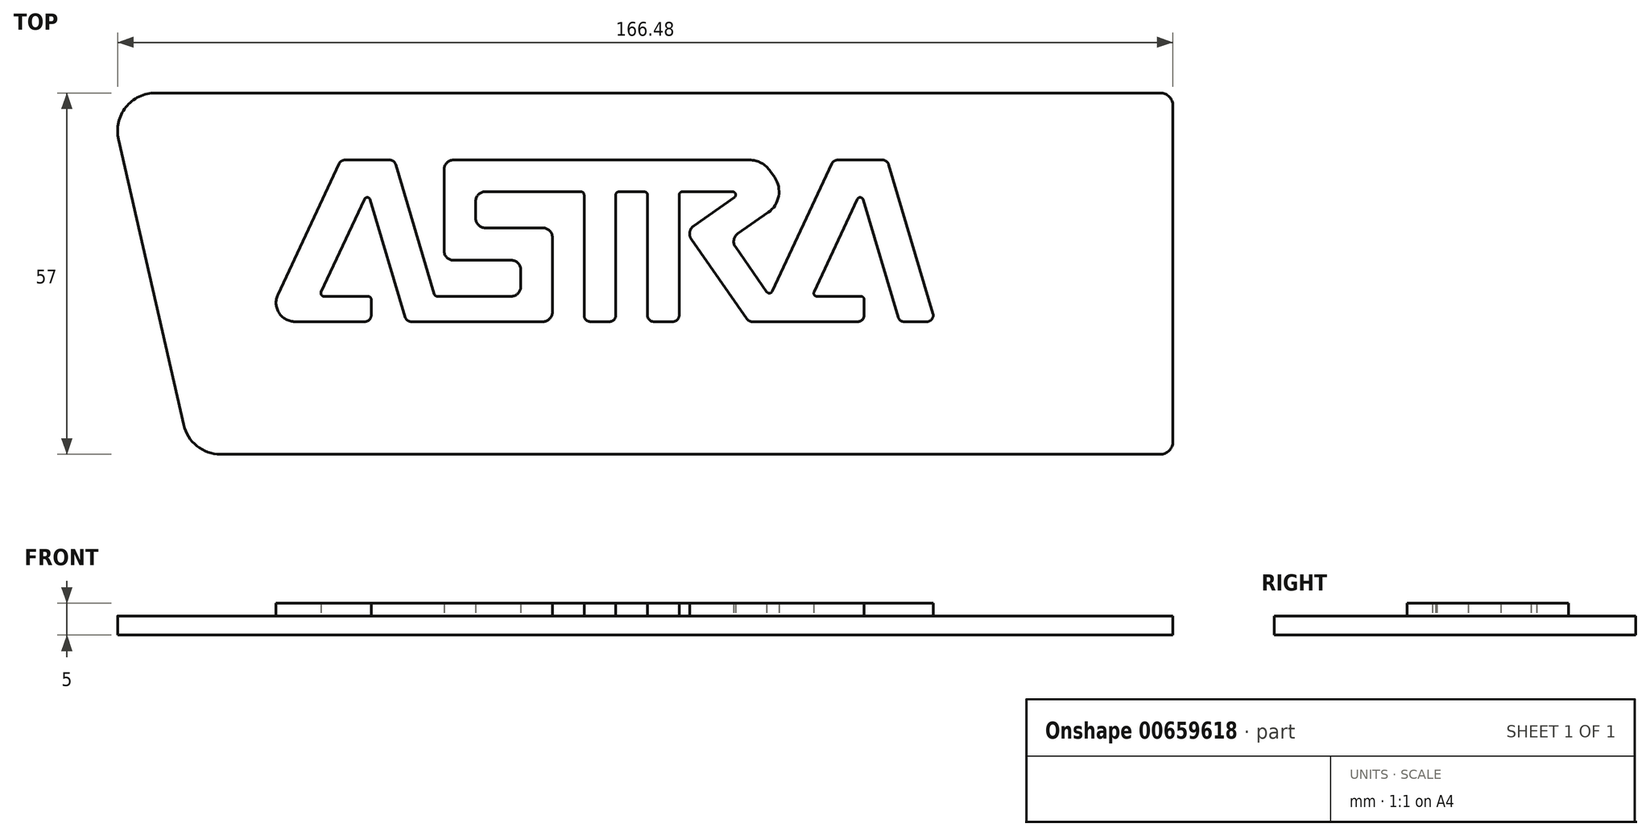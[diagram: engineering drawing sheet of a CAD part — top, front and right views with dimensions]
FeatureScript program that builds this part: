
annotation { "Feature Type Name" : "Feature", "Feature Type Description" : "" }
export const myFeature = defineFeature(function(context is Context, id is Id, definition is map)
    precondition{}
    {
        {
            var Q0;
            Q0=qCreatedBy(makeId("Top.planeOp"),FACE);
            var sketch = newSketch(context, id + "F0", { "sketchPlane" : qUnion([Q0])});
            skLineSegment(sketch, "E0", {"start": v(-73.7, 12.8) * mm, "end": v(84.77, 12.8) * mm});
            skLineSegment(sketch, "E1", {"start": v(86.77, 10.8) * mm, "end": v(86.77, -42.2) * mm});
            skLineSegment(sketch, "E2", {"start": v(84.77, -44.2) * mm, "end": v(-63.44, -44.2) * mm});
            skLineSegment(sketch, "E3", {"start": v(-69.3, -39.53) * mm, "end": v(-79.56, 5.47) * mm});
            skPoint(sketch, "E4.visualSharp", {"position": v(-81.23, 12.8) * mm});
            skArc(sketch, "E4.filletArc", {"start": v(-73.7, 12.8) * mm, "mid": v(-78.4, 10.55) * mm, "end": v(-79.56, 5.47) * mm});
            skPoint(sketch, "E5.visualSharp", {"position": v(-68.23, -44.2) * mm});
            skArc(sketch, "E5.filletArc", {"start": v(-69.3, -39.53) * mm, "mid": v(-67.18, -42.89) * mm, "end": v(-63.44, -44.2) * mm});
            skPoint(sketch, "E6.visualSharp", {"position": v(86.77, 12.8) * mm});
            skArc(sketch, "E6.filletArc", {"start": v(86.77, 10.8) * mm, "mid": v(86.19, 12.22) * mm, "end": v(84.77, 12.8) * mm});
            skPoint(sketch, "E7.visualSharp", {"position": v(86.77, -44.2) * mm});
            skArc(sketch, "E7.filletArc", {"start": v(84.77, -44.2) * mm, "mid": v(86.19, -43.6) * mm, "end": v(86.77, -42.2) * mm});
            skLineSegment(sketch, "E8", {"start": v(-54.42, -19) * mm, "end": v(-44.77, 1.65) * mm});
            skLineSegment(sketch, "E9", {"start": v(-43.86, 2.22) * mm, "end": v(-36.78, 2.22) * mm});
            skLineSegment(sketch, "E10", {"start": v(-51.7, -23.28) * mm, "end": v(-40.69, -23.28) * mm});
            skLineSegment(sketch, "E11", {"start": v(-39.69, -22.28) * mm, "end": v(-39.69, -19.78) * mm});
            skLineSegment(sketch, "E12", {"start": v(-40.19, -19.28) * mm, "end": v(-47.14, -19.28) * mm});
            skLineSegment(sketch, "E13", {"start": v(-47.6, -18.57) * mm, "end": v(-40.77, -3.97) * mm});
            skLineSegment(sketch, "E14", {"start": v(-39.84, -4.04) * mm, "end": v(-34.32, -22.56) * mm});
            skLineSegment(sketch, "E15", {"start": v(-35.82, 1.5) * mm, "end": v(-29.74, -18.92) * mm});
            skLineSegment(sketch, "E16", {"start": v(-29.27, -19.28) * mm, "end": v(-17.61, -19.28) * mm});
            skLineSegment(sketch, "E17", {"start": v(-33.37, -23.28) * mm, "end": v(-12.61, -23.28) * mm});
            skLineSegment(sketch, "E18", {"start": v(-16.11, -17.78) * mm, "end": v(-16.11, -15.08) * mm});
            skLineSegment(sketch, "E19", {"start": v(-17.61, -13.58) * mm, "end": v(-26.7, -13.58) * mm});
            skLineSegment(sketch, "E20", {"start": v(-28.2, -12.08) * mm, "end": v(-28.2, 0.72) * mm});
            skLineSegment(sketch, "E21", {"start": v(-11.11, -21.78) * mm, "end": v(-11.11, -9.98) * mm});
            skLineSegment(sketch, "E22", {"start": v(-12.61, -8.48) * mm, "end": v(-21.7, -8.48) * mm});
            skLineSegment(sketch, "E23", {"start": v(-23.2, -6.98) * mm, "end": v(-23.2, -4.28) * mm});
            skLineSegment(sketch, "E24", {"start": v(-21.7, -2.78) * mm, "end": v(-6.61, -2.78) * mm});
            skLineSegment(sketch, "E25", {"start": v(-6.11, -3.28) * mm, "end": v(-6.11, -22.28) * mm});
            skLineSegment(sketch, "E26", {"start": v(-5.11, -23.28) * mm, "end": v(-2.11, -23.28) * mm});
            skLineSegment(sketch, "E27", {"start": v(-1.11, -22.28) * mm, "end": v(-1.11, -3.28) * mm});
            skLineSegment(sketch, "E28", {"start": v(-0.61, -2.78) * mm, "end": v(3.39, -2.78) * mm});
            skLineSegment(sketch, "E29", {"start": v(3.89, -3.28) * mm, "end": v(3.89, -22.28) * mm});
            skLineSegment(sketch, "E30", {"start": v(4.89, -23.28) * mm, "end": v(7.89, -23.28) * mm});
            skLineSegment(sketch, "E31", {"start": v(8.89, -22.28) * mm, "end": v(8.89, -3.28) * mm});
            skLineSegment(sketch, "E32", {"start": v(9.39, -2.78) * mm, "end": v(17.3, -2.78) * mm});
            skLineSegment(sketch, "E33", {"start": v(17.59, -3.69) * mm, "end": v(11.17, -8.16) * mm});
            skLineSegment(sketch, "E34", {"start": v(10.8, -10.25) * mm, "end": v(19.6, -22.85) * mm});
            skLineSegment(sketch, "E35", {"start": v(-26.7, 2.22) * mm, "end": v(19.96, 2.22) * mm});
            skPoint(sketch, "E36.visualSharp", {"position": v(9.94, -9.02) * mm});
            skArc(sketch, "E36.filletArc", {"start": v(11.17, -8.16) * mm, "mid": v(10.56, -9.13) * mm, "end": v(10.8, -10.25) * mm});
            skPoint(sketch, "E37.visualSharp", {"position": v(16.9, -10.26) * mm});
            skPoint(sketch, "E38.visualSharp", {"position": v(34.8, 2.22) * mm});
            skLineSegment(sketch, "E39", {"start": v(23.57, -18.5) * mm, "end": v(32.99, 1.65) * mm});
            skLineSegment(sketch, "E40", {"start": v(33.9, 2.22) * mm, "end": v(40.97, 2.22) * mm});
            skLineSegment(sketch, "E41", {"start": v(20.42, -23.28) * mm, "end": v(37.06, -23.28) * mm});
            skLineSegment(sketch, "E42", {"start": v(38.06, -22.28) * mm, "end": v(38.06, -19.78) * mm});
            skLineSegment(sketch, "E43", {"start": v(37.56, -19.28) * mm, "end": v(30.61, -19.28) * mm});
            skLineSegment(sketch, "E44", {"start": v(30.16, -18.57) * mm, "end": v(36.98, -3.97) * mm});
            skLineSegment(sketch, "E45", {"start": v(37.92, -4.04) * mm, "end": v(43.42, -22.56) * mm});
            skLineSegment(sketch, "E46", {"start": v(41.93, 1.5) * mm, "end": v(48.92, -22) * mm});
            skLineSegment(sketch, "E47", {"start": v(47.96, -23.28) * mm, "end": v(44.38, -23.28) * mm});
            skPoint(sketch, "E48.visualSharp", {"position": v(-44.5, 2.22) * mm});
            skArc(sketch, "E48.filletArc", {"start": v(-43.86, 2.22) * mm, "mid": v(-44.4, 2.07) * mm, "end": v(-44.77, 1.65) * mm});
            skPoint(sketch, "E49.visualSharp", {"position": v(-36.03, 2.22) * mm});
            skArc(sketch, "E49.filletArc", {"start": v(-35.82, 1.5) * mm, "mid": v(-36.18, 2.02) * mm, "end": v(-36.78, 2.22) * mm});
            skPoint(sketch, "E50.visualSharp", {"position": v(-34.11, -23.28) * mm});
            skArc(sketch, "E50.filletArc", {"start": v(-34.32, -22.56) * mm, "mid": v(-33.96, -23.08) * mm, "end": v(-33.37, -23.28) * mm});
            skPoint(sketch, "E51.visualSharp", {"position": v(-6.11, -23.28) * mm});
            skArc(sketch, "E51.filletArc", {"start": v(-6.11, -22.28) * mm, "mid": v(-5.82, -22.98) * mm, "end": v(-5.11, -23.28) * mm});
            skPoint(sketch, "E52.visualSharp", {"position": v(-1.11, -23.28) * mm});
            skArc(sketch, "E52.filletArc", {"start": v(-2.11, -23.28) * mm, "mid": v(-1.4, -22.98) * mm, "end": v(-1.11, -22.28) * mm});
            skPoint(sketch, "E53.visualSharp", {"position": v(3.89, -23.28) * mm});
            skArc(sketch, "E53.filletArc", {"start": v(3.89, -22.28) * mm, "mid": v(4.18, -22.98) * mm, "end": v(4.89, -23.28) * mm});
            skPoint(sketch, "E54.visualSharp", {"position": v(8.89, -23.28) * mm});
            skArc(sketch, "E54.filletArc", {"start": v(7.89, -23.28) * mm, "mid": v(8.6, -22.98) * mm, "end": v(8.89, -22.28) * mm});
            skPoint(sketch, "E55.visualSharp", {"position": v(-39.69, -23.28) * mm});
            skArc(sketch, "E55.filletArc", {"start": v(-40.69, -23.28) * mm, "mid": v(-39.98, -22.98) * mm, "end": v(-39.69, -22.28) * mm});
            skPoint(sketch, "E56.visualSharp", {"position": v(19.9, -23.28) * mm});
            skArc(sketch, "E56.filletArc", {"start": v(19.6, -22.85) * mm, "mid": v(19.96, -23.16) * mm, "end": v(20.42, -23.28) * mm});
            skPoint(sketch, "E57.visualSharp", {"position": v(38.06, -23.28) * mm});
            skArc(sketch, "E57.filletArc", {"start": v(37.06, -23.28) * mm, "mid": v(37.77, -22.98) * mm, "end": v(38.06, -22.28) * mm});
            skPoint(sketch, "E58.visualSharp", {"position": v(43.64, -23.28) * mm});
            skArc(sketch, "E58.filletArc", {"start": v(43.42, -22.56) * mm, "mid": v(43.79, -23.08) * mm, "end": v(44.38, -23.28) * mm});
            skPoint(sketch, "E59.visualSharp", {"position": v(49.3, -23.28) * mm});
            skArc(sketch, "E59.filletArc", {"start": v(47.96, -23.28) * mm, "mid": v(48.76, -22.87) * mm, "end": v(48.92, -22) * mm});
            skPoint(sketch, "E60.visualSharp", {"position": v(41.72, 2.22) * mm});
            skArc(sketch, "E60.filletArc", {"start": v(41.93, 1.5) * mm, "mid": v(41.57, 2.02) * mm, "end": v(40.97, 2.22) * mm});
            skPoint(sketch, "E61.visualSharp", {"position": v(33.26, 2.22) * mm});
            skArc(sketch, "E61.filletArc", {"start": v(33.9, 2.22) * mm, "mid": v(33.35, 2.07) * mm, "end": v(32.99, 1.65) * mm});
            skPoint(sketch, "E62.visualSharp", {"position": v(-56.42, -23.28) * mm});
            skArc(sketch, "E62.filletArc", {"start": v(-54.42, -19) * mm, "mid": v(-54.24, -21.89) * mm, "end": v(-51.7, -23.28) * mm});
            skPoint(sketch, "E63.visualSharp", {"position": v(-28.2, -13.58) * mm});
            skArc(sketch, "E63.filletArc", {"start": v(-28.2, -12.08) * mm, "mid": v(-27.77, -13.14) * mm, "end": v(-26.7, -13.58) * mm});
            skPoint(sketch, "E64.visualSharp", {"position": v(-28.2, 2.22) * mm});
            skArc(sketch, "E64.filletArc", {"start": v(-26.7, 2.22) * mm, "mid": v(-27.77, 1.78) * mm, "end": v(-28.2, 0.72) * mm});
            skPoint(sketch, "E65.visualSharp", {"position": v(-23.2, -2.78) * mm});
            skArc(sketch, "E65.filletArc", {"start": v(-21.7, -2.78) * mm, "mid": v(-22.77, -3.22) * mm, "end": v(-23.2, -4.28) * mm});
            skPoint(sketch, "E66.visualSharp", {"position": v(-23.2, -8.48) * mm});
            skArc(sketch, "E66.filletArc", {"start": v(-23.2, -6.98) * mm, "mid": v(-22.77, -8.04) * mm, "end": v(-21.7, -8.48) * mm});
            skPoint(sketch, "E67.visualSharp", {"position": v(-11.11, -8.48) * mm});
            skArc(sketch, "E67.filletArc", {"start": v(-11.11, -9.98) * mm, "mid": v(-11.55, -8.92) * mm, "end": v(-12.61, -8.48) * mm});
            skPoint(sketch, "E68.visualSharp", {"position": v(-16.11, -13.58) * mm});
            skArc(sketch, "E68.filletArc", {"start": v(-16.11, -15.08) * mm, "mid": v(-16.55, -14.02) * mm, "end": v(-17.61, -13.58) * mm});
            skPoint(sketch, "E69.visualSharp", {"position": v(-16.11, -19.28) * mm});
            skArc(sketch, "E69.filletArc", {"start": v(-17.61, -19.28) * mm, "mid": v(-16.55, -18.84) * mm, "end": v(-16.11, -17.78) * mm});
            skPoint(sketch, "E70.visualSharp", {"position": v(-11.11, -23.28) * mm});
            skArc(sketch, "E70.filletArc", {"start": v(-12.61, -23.28) * mm, "mid": v(-11.55, -22.84) * mm, "end": v(-11.11, -21.78) * mm});
            skPoint(sketch, "E71.visualSharp", {"position": v(37.54, -2.78) * mm});
            skArc(sketch, "E71.filletArc", {"start": v(37.92, -4.04) * mm, "mid": v(37.47, -3.68) * mm, "end": v(36.98, -3.97) * mm});
            skPoint(sketch, "E72.visualSharp", {"position": v(29.83, -19.28) * mm});
            skArc(sketch, "E72.filletArc", {"start": v(30.16, -18.57) * mm, "mid": v(30.2, -19.05) * mm, "end": v(30.61, -19.28) * mm});
            skPoint(sketch, "E73.visualSharp", {"position": v(38.06, -19.28) * mm});
            skArc(sketch, "E73.filletArc", {"start": v(38.06, -19.78) * mm, "mid": v(37.92, -19.42) * mm, "end": v(37.56, -19.28) * mm});
            skPoint(sketch, "E74.visualSharp", {"position": v(-40.21, -2.78) * mm});
            skArc(sketch, "E74.filletArc", {"start": v(-39.84, -4.04) * mm, "mid": v(-40.28, -3.68) * mm, "end": v(-40.77, -3.97) * mm});
            skPoint(sketch, "E75.visualSharp", {"position": v(-47.93, -19.28) * mm});
            skArc(sketch, "E75.filletArc", {"start": v(-47.6, -18.57) * mm, "mid": v(-47.56, -19.05) * mm, "end": v(-47.14, -19.28) * mm});
            skPoint(sketch, "E76.visualSharp", {"position": v(-39.69, -19.28) * mm});
            skArc(sketch, "E76.filletArc", {"start": v(-39.69, -19.78) * mm, "mid": v(-39.83, -19.42) * mm, "end": v(-40.19, -19.28) * mm});
            skPoint(sketch, "E77.visualSharp", {"position": v(-29.64, -19.28) * mm});
            skArc(sketch, "E77.filletArc", {"start": v(-29.74, -18.92) * mm, "mid": v(-29.56, -19.18) * mm, "end": v(-29.27, -19.28) * mm});
            skPoint(sketch, "E78.visualSharp", {"position": v(-6.11, -2.78) * mm});
            skArc(sketch, "E78.filletArc", {"start": v(-6.11, -3.28) * mm, "mid": v(-6.26, -2.92) * mm, "end": v(-6.61, -2.78) * mm});
            skPoint(sketch, "E79.visualSharp", {"position": v(-1.11, -2.78) * mm});
            skArc(sketch, "E79.filletArc", {"start": v(-0.61, -2.78) * mm, "mid": v(-0.97, -2.92) * mm, "end": v(-1.11, -3.28) * mm});
            skPoint(sketch, "E80.visualSharp", {"position": v(3.89, -2.78) * mm});
            skArc(sketch, "E80.filletArc", {"start": v(3.89, -3.28) * mm, "mid": v(3.74, -2.92) * mm, "end": v(3.39, -2.78) * mm});
            skPoint(sketch, "E81.visualSharp", {"position": v(8.89, -2.78) * mm});
            skArc(sketch, "E81.filletArc", {"start": v(9.39, -2.78) * mm, "mid": v(9.03, -2.92) * mm, "end": v(8.89, -3.28) * mm});
            skPoint(sketch, "E82.visualSharp", {"position": v(18.89, -2.78) * mm});
            skArc(sketch, "E82.filletArc", {"start": v(17.59, -3.69) * mm, "mid": v(17.78, -3.13) * mm, "end": v(17.3, -2.78) * mm});
            skPoint(sketch, "E83.visualSharp", {"position": v(23.2, -19.28) * mm});
            skArc(sketch, "E83.filletArc", {"start": v(22.7, -18.56) * mm, "mid": v(23.16, -18.78) * mm, "end": v(23.57, -18.5) * mm});
            skLineSegment(sketch, "E84", {"start": v(23.95, -0.52) * mm, "end": v(23.27, 0.48) * mm});
            skLineSegment(sketch, "E85", {"start": v(22.7, -18.56) * mm, "end": v(17.76, -11.49) * mm});
            skLineSegment(sketch, "E86", {"start": v(22.93, -6.05) * mm, "end": v(18.13, -9.4) * mm});
            skArc(sketch, "E87.filletArc", {"start": v(18.13, -9.4) * mm, "mid": v(17.52, -10.37) * mm, "end": v(17.76, -11.49) * mm});
            skPoint(sketch, "E88.visualSharp", {"position": v(22.08, 2.22) * mm});
            skArc(sketch, "E88.filletArc", {"start": v(23.27, 0.48) * mm, "mid": v(21.83, 1.76) * mm, "end": v(19.96, 2.22) * mm});
            skPoint(sketch, "E89.visualSharp", {"position": v(26.17, -3.78) * mm});
            skArc(sketch, "E89.filletArc", {"start": v(22.93, -6.05) * mm, "mid": v(24.57, -3.49) * mm, "end": v(23.95, -0.52) * mm});
            skSolve(sketch);
        }
        {
            var Q0;
            Q0 = qSketchRegion(id + "F0", true);
            extrude(context, id + "F1", {"entities" : qUnion([Q0]), "depth" : 3 * mm, "offsetDistance" : 25 * mm});
        }
        {
            var Q0;
            Q0=makeQuery(id+"F0.imprint","IMPRINT",FACE,{"disambiguationData":[TD([[makeQuery(id+"F0.imprint","IMPRINT",EDGE,{"derivedFrom":sQuery(id+"F0.wireOp",EDGE,"E8")}),-1.0]])]});
            extrude(context, id + "F2", {"entities" : qUnion([Q0]), "operationType" : NewBodyOperationType.ADD, "depth" : 5 * mm, "offsetDistance" : 25 * mm});
        }
    });
